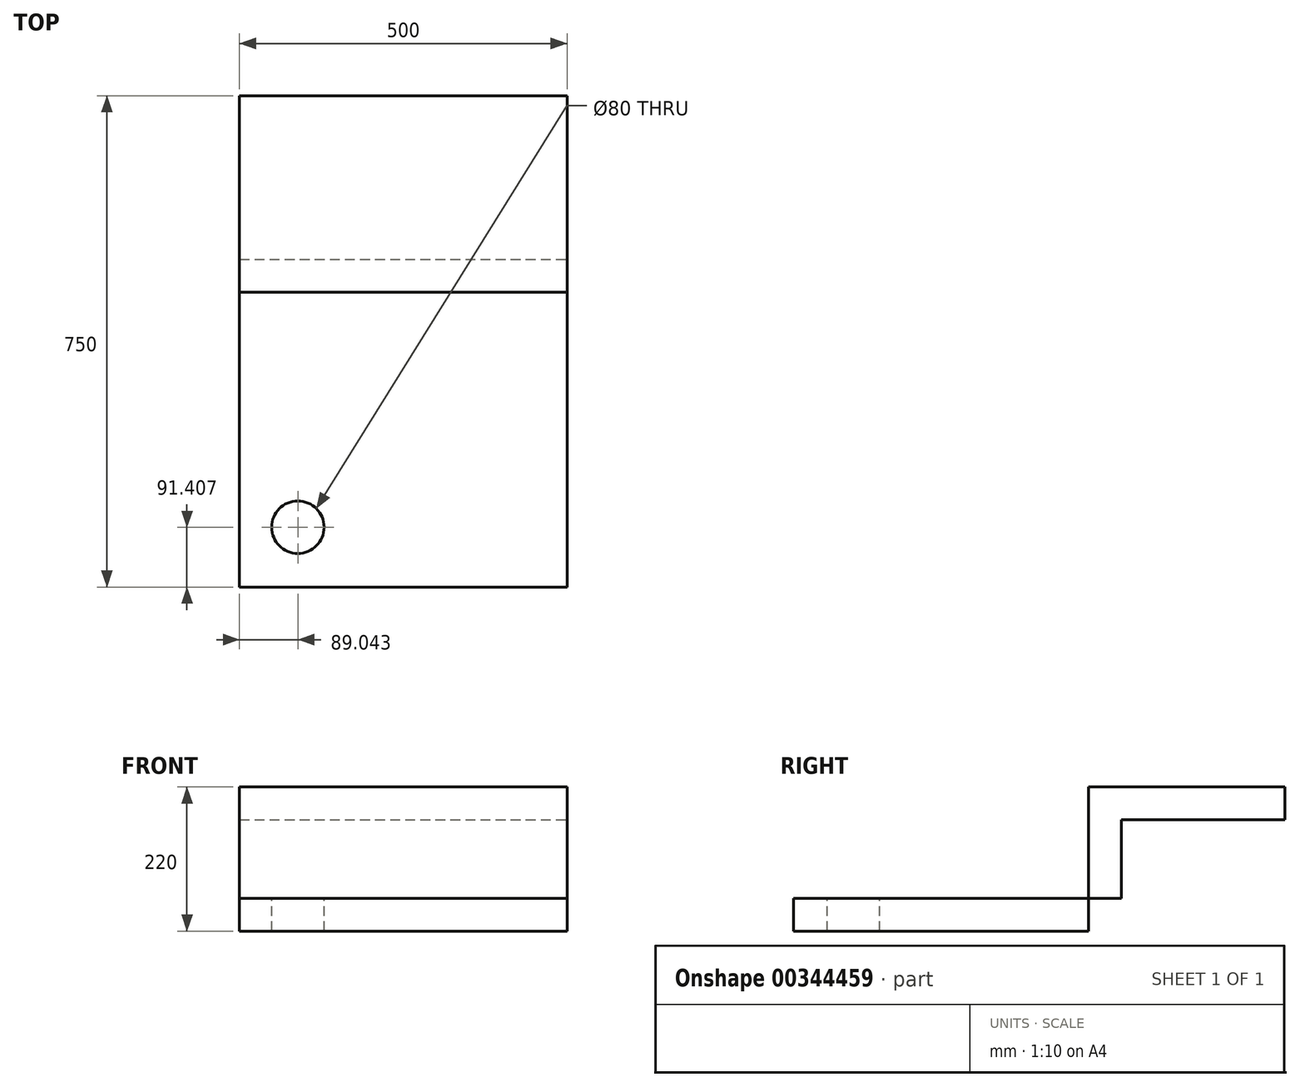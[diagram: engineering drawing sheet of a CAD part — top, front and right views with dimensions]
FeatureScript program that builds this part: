
annotation { "Feature Type Name" : "Feature", "Feature Type Description" : "" }
export const myFeature = defineFeature(function(context is Context, id is Id, definition is map)
    precondition{}
    {
        {
            var Q0;
            Q0=qCreatedBy(makeId("Front.planeOp"),FACE);
            var sketch = newSketch(context, id + "F0", { "sketchPlane" : qUnion([Q0])});
            skLineSegment(sketch, "E0", {"start": v(0, 0) * mm, "end": v(-500, 0) * mm});
            skLineSegment(sketch, "E1", {"start": v(-500, 0) * mm, "end": v(-500, 50) * mm});
            skLineSegment(sketch, "E2", {"start": v(-500, 50) * mm, "end": v(0, 50) * mm});
            skLineSegment(sketch, "E3", {"start": v(0, 50) * mm, "end": v(0, 0) * mm});
            skSolve(sketch);
        }
        {
            var Q0;
            Q0 = qSketchRegion(id + "F0", true);
            var Q1;
            Q1=makeQuery(id+"F0.imprint","IMPRINT",FACE,{"disambiguationData":[TD([[makeQuery(id+"F0.imprint","IMPRINT",EDGE,{"derivedFrom":sQuery(id+"F0.wireOp",EDGE,"E0")}),-1.0]])]});
            extrude(context, id + "F1", {"entities" : qUnion([Q0, Q1]), "oppositeDirection" : true, "depth" : 450 * mm});
        }
        {
            var Q0;
            Q0=makeQuery(id+"F1.opExtrude","CAP_FACE",FACE,{"disambiguationData":[OSD([sQuery(id+"F0.wireOp",EDGE,"E0"),sQuery(id+"F0.wireOp",EDGE,"E1"),sQuery(id+"F0.wireOp",EDGE,"E2"),sQuery(id+"F0.wireOp",EDGE,"E3")])],"isStart":false});
            var sketch = newSketch(context, id + "F2", { "sketchPlane" : qUnion([Q0])});
            skLineSegment(sketch, "E4", {"start": v(500, 50) * mm, "end": v(500, 220) * mm});
            skLineSegment(sketch, "E5", {"start": v(500, 220) * mm, "end": v(0, 220) * mm});
            skLineSegment(sketch, "E6", {"start": v(0, 220) * mm, "end": v(0, 50) * mm});
            skSolve(sketch);
        }
        {
            var Q0;
            Q0=makeQuery(id+"F2.imprint","IMPRINT",FACE,{"disambiguationData":[TD([[makeQuery(id+"F2.imprint","IMPRINT",EDGE,{"derivedFrom":sQuery(id+"F2.wireOp",EDGE,"E4")}),1.0]])]});
            extrude(context, id + "F3", {"entities" : qUnion([Q0]), "depth" : 50 * mm});
        }
        {
            var Q0;
            Q0=makeQuery(id+"F3.opExtrude","SWEPT_FACE",FACE,{"disambiguationData":[OSD([sQuery(id+"F2.wireOp",EDGE,"E5")])]});
            var sketch = newSketch(context, id + "F4", { "sketchPlane" : qUnion([Q0])});
            skLineSegment(sketch, "E7", {"start": v(-500, 500) * mm, "end": v(-500, 750) * mm});
            skLineSegment(sketch, "E8", {"start": v(-500, 750) * mm, "end": v(0, 750) * mm});
            skLineSegment(sketch, "E9", {"start": v(0, 750) * mm, "end": v(0, 500) * mm});
            skSolve(sketch);
        }
        {
            var Q0;
            Q0=makeQuery(id+"F4.imprint","IMPRINT",FACE,{"disambiguationData":[TD([[makeQuery(id+"F4.imprint","IMPRINT",EDGE,{"derivedFrom":sQuery(id+"F4.wireOp",EDGE,"E7")}),-1.0]])]});
            extrude(context, id + "F5", {"entities" : qUnion([Q0]), "operationType" : NewBodyOperationType.ADD, "oppositeDirection" : true, "depth" : 50 * mm});
        }
        {
            var Q0;
            Q0=makeQuery(id+"F1.opExtrude","SWEPT_FACE",FACE,{"disambiguationData":[OSD([sQuery(id+"F0.wireOp",EDGE,"E2")])]});
            var sketch = newSketch(context, id + "F6", { "sketchPlane" : qUnion([Q0])});
            skCircle(sketch, "E10", {"center": v(-410.96, 91.4) * mm, "radius": 40 * mm});
            skSolve(sketch);
        }
        {
            var Q0;
            Q0=sQuery(id+"F6.wireOp",VERTEX,"E10.center");
            var Q1;
            Q1=makeQuery(id+"F1.opExtrude","SWEPT_BODY",BODY,{"disambiguationData":[OSD([sQuery(id+"F0.wireOp",EDGE,"E0"),sQuery(id+"F0.wireOp",EDGE,"E1"),sQuery(id+"F0.wireOp",EDGE,"E2"),sQuery(id+"F0.wireOp",EDGE,"E3")])]});
            hole(context, id + "F7", {"style" : HoleStyle.SIMPLE, "endStyle" : HoleEndStyle.THROUGH, "holeDiameter" : 80 * mm, "isTappedThrough" : true, "tappedDepth" : 12 * mm, "tapClearance" : 3, "locations" : qUnion([Q0]), "scope" : qUnion([Q1])});
        }
    });
